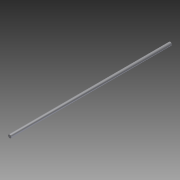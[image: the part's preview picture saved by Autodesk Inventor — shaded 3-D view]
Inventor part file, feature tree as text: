
AUTODESK INVENTOR PART (.ipt)
format: ipt  version: 2012 (Build 160160000, 160)  size: 61,952 bytes
history: native  units: in
note: dims shown in document units (in); Inventor stores cm internally (conversion verified against a paired STEP export)
features: extrude x1, sketch x1
ambient origin geometry x8: Origin, YZ Plane, XZ Plane, XY Plane, X Axis, Y Axis, Z Axis, Center Point
bodies: Solid1 (feature_tree)
feature tree (2):
  extrude  "Extrusion1"  Depth=25.0in TaperAngle=0.0deg
  sketch  "Sketch1"  dims[d0=0.5in d1=25.0in d2=0.0in]
